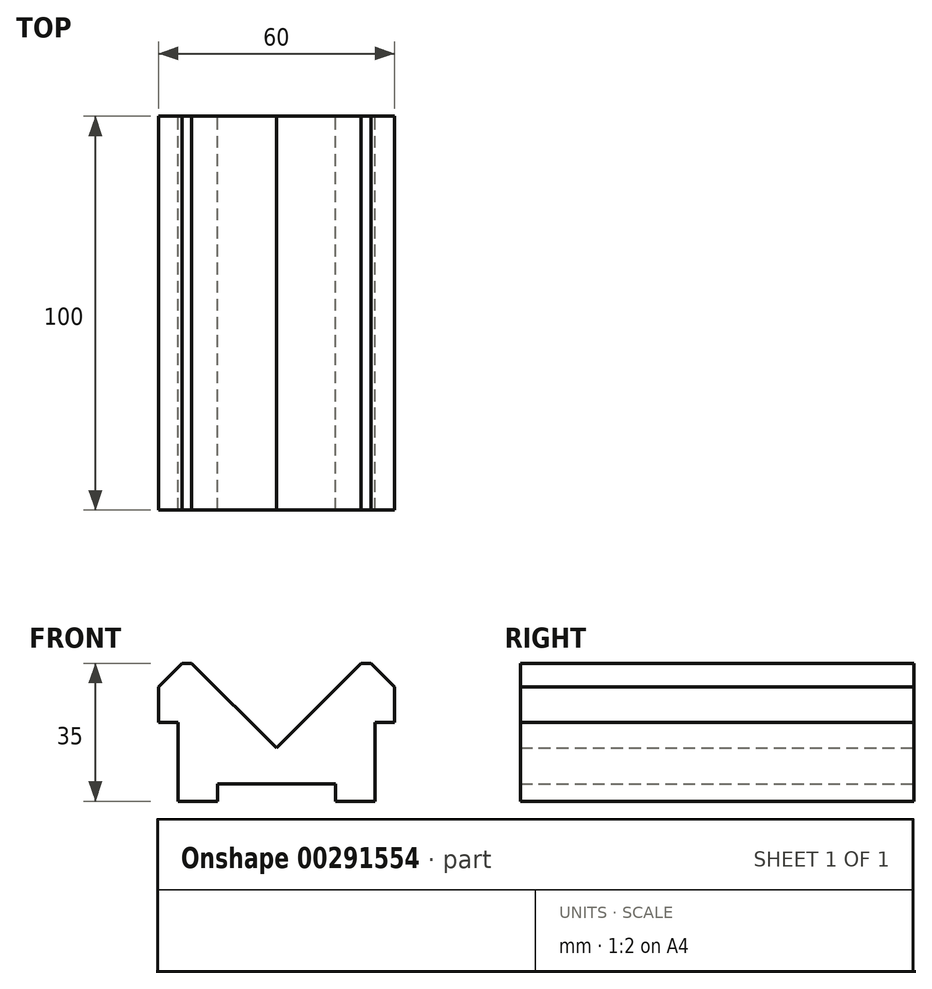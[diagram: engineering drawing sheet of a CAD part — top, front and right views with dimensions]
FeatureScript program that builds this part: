
annotation { "Feature Type Name" : "Feature", "Feature Type Description" : "" }
export const myFeature = defineFeature(function(context is Context, id is Id, definition is map)
    precondition{}
    {
        {
            var Q0;
            Q0=qCreatedBy(makeId("Front.planeOp"),FACE);
            var sketch = newSketch(context, id + "F0", { "sketchPlane" : qUnion([Q0])});
            skPoint(sketch, "E0.end.orphan", {"position": v(5, 0) * mm});
            skPoint(sketch, "E0.start.orphan", {"position": v(0, -2.01) * mm});
            skLineSegment(sketch, "E1", {"start": v(0, 0) * mm, "end": v(15, 0) * mm});
            skPoint(sketch, "E2", {"position": v(55, 0) * mm});
            skPoint(sketch, "E3", {"position": v(15, 0) * mm});
            skPoint(sketch, "E4", {"position": v(45, 0) * mm});
            skPoint(sketch, "E5.end.orphan", {"position": v(5, 35) * mm});
            skPoint(sketch, "E6.end.orphan", {"position": v(55, 35) * mm});
            skLineSegment(sketch, "E7", {"start": v(5, 0) * mm, "end": v(5, 20) * mm});
            skLineSegment(sketch, "E8", {"start": v(55, 0) * mm, "end": v(55, 20) * mm});
            skLineSegment(sketch, "E9", {"start": v(5, 20) * mm, "end": v(0, 20) * mm});
            skLineSegment(sketch, "E10", {"start": v(0, 20) * mm, "end": v(0, 29) * mm});
            skLineSegment(sketch, "E11", {"start": v(60, 19.25) * mm, "end": v(60, 20) * mm});
            skLineSegment(sketch, "E12", {"start": v(55, 20) * mm, "end": v(60, 20) * mm});
            skPoint(sketch, "E12.endSnap0", {"position": v(60, 19.25) * mm});
            skPoint(sketch, "E13.orphan", {"position": v(60, 38.5) * mm});
            skLineSegment(sketch, "E14", {"start": v(60, 20) * mm, "end": v(60, 29) * mm});
            skLineSegment(sketch, "E15", {"start": v(0, 29) * mm, "end": v(6, 35) * mm});
            skLineSegment(sketch, "E16", {"start": v(15, 0) * mm, "end": v(15, 4.45) * mm});
            skLineSegment(sketch, "E17", {"start": v(45, 0) * mm, "end": v(45, 4.45) * mm});
            skLineSegment(sketch, "E18", {"start": v(15, 4.45) * mm, "end": v(45, 4.45) * mm});
            skPoint(sketch, "E19.orphan", {"position": v(45, 4.77) * mm});
            skLineSegment(sketch, "E20.trimOffspring", {"start": v(45, 0) * mm, "end": v(60, 0) * mm});
            skLineSegment(sketch, "E21", {"start": v(27.5, 0) * mm, "end": v(32.5, 0) * mm, "construction": true});
            skPoint(sketch, "E22", {"position": v(30, 0) * mm});
            skLineSegment(sketch, "E23", {"start": v(30, 0) * mm, "end": v(27.5, 0) * mm});
            skLineSegment(sketch, "E24", {"start": v(30, 0) * mm, "end": v(32.5, 0) * mm});
            skPoint(sketch, "E25", {"position": v(27.5, 4.45) * mm});
            skPoint(sketch, "E26", {"position": v(32.5, 4.45) * mm});
            skPoint(sketch, "E27.end.orphan", {"position": v(55, 32.15) * mm});
            skLineSegment(sketch, "E28", {"start": v(60, 29) * mm, "end": v(54, 35) * mm});
            skLineSegment(sketch, "E29", {"start": v(6, 35) * mm, "end": v(8.5, 35) * mm, "construction": true});
            skLineSegment(sketch, "E30", {"start": v(6, 35) * mm, "end": v(8.5, 35) * mm});
            skLineSegment(sketch, "E31", {"start": v(54, 35) * mm, "end": v(51.5, 35) * mm});
            skLineSegment(sketch, "E32.trimOffspring", {"start": v(51.5, 35) * mm, "end": v(54, 35) * mm, "construction": true});
            skPoint(sketch, "E33.end.orphan", {"position": v(8.85, 0) * mm});
            skPoint(sketch, "E34.orphan", {"position": v(8.85, 35) * mm});
            skPoint(sketch, "E35", {"position": v(54, 12) * mm});
            skLineSegment(sketch, "E36", {"start": v(8.5, 35) * mm, "end": v(30, 13.5) * mm, "construction": true});
            skLineSegment(sketch, "E37", {"start": v(30, 13.5) * mm, "end": v(32.5, 16) * mm, "construction": true});
            skLineSegment(sketch, "E38", {"start": v(8.5, 35) * mm, "end": v(8.85, 35) * mm, "construction": true});
            skLineSegment(sketch, "E39", {"start": v(8.5, 35) * mm, "end": v(30, 13.5) * mm});
            skLineSegment(sketch, "E40", {"start": v(30, 13.5) * mm, "end": v(32.5, 16) * mm});
            skLineSegment(sketch, "E41.trimOffspring", {"start": v(27.5, 15.97) * mm, "end": v(27.5, 16) * mm, "construction": true});
            skPoint(sketch, "E42.end.orphan", {"position": v(54, 0) * mm});
            skLineSegment(sketch, "E43", {"start": v(32.5, 16) * mm, "end": v(51.5, 35) * mm});
            skLineSegment(sketch, "E44", {"start": v(6, 35) * mm, "end": v(19.58, 35) * mm, "construction": true});
            skLineSegment(sketch, "E45", {"start": v(19.58, 35) * mm, "end": v(51.5, 35) * mm, "construction": true});
            skLineSegment(sketch, "E46", {"start": v(30, 0) * mm, "end": v(30, 48.86) * mm, "construction": true});
            skLineSegment(sketch, "E47", {"start": v(30, 48.86) * mm, "end": v(30, -52.43) * mm, "construction": true});
            skSolve(sketch);
        }
        {
            var Q0;
            {var subQ3=sQuery(id+"F0.wireOp",EDGE,"E7");Q0=makeQuery(id+"F0.imprint","IMPRINT",FACE,{"disambiguationData":[TD([[makeQuery(id+"F0.imprint","IMPRINT",EDGE,{"derivedFrom":subQ3}),-1.0]])]});}
            extrude(context, id + "F1", {"entities" : qUnion([Q0]), "depth" : 100 * mm});
        }
    });
